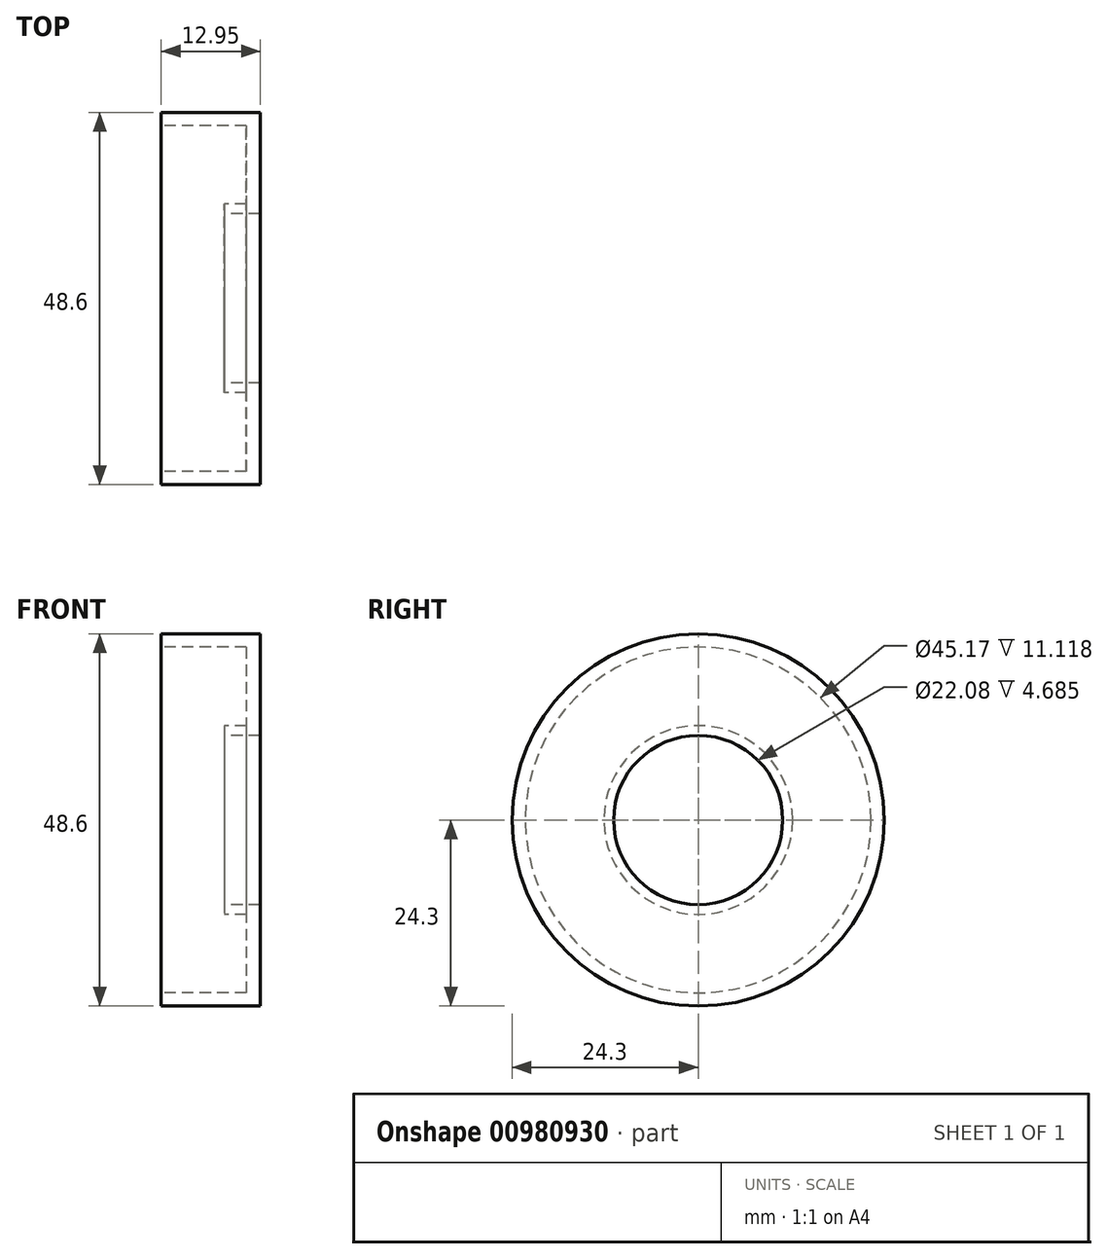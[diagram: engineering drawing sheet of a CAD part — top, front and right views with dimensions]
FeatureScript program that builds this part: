
annotation { "Feature Type Name" : "Feature", "Feature Type Description" : "" }
export const myFeature = defineFeature(function(context is Context, id is Id, definition is map)
    precondition{}
    {
        {
            var Q0;
            Q0=qCreatedBy(makeId("Front.planeOp"),FACE);
            var sketch = newSketch(context, id + "F0", { "sketchPlane" : qUnion([Q0])});
            skLineSegment(sketch, "E0", {"start": v(-81.51, 0) * mm, "end": v(83.97, 0) * mm, "construction": true});
            skLineSegment(sketch, "E1", {"start": v(-12.95, 24.3) * mm, "end": v(0, 24.3) * mm});
            skLineSegment(sketch, "E2", {"start": v(0, 24.3) * mm, "end": v(0, 11.04) * mm});
            skLineSegment(sketch, "E3", {"start": v(0, 11.04) * mm, "end": v(-4.69, 11.04) * mm});
            skLineSegment(sketch, "E4", {"start": v(-4.69, 11.04) * mm, "end": v(-4.69, 12.32) * mm});
            skLineSegment(sketch, "E5", {"start": v(-4.69, 12.32) * mm, "end": v(-1.83, 12.32) * mm});
            skLineSegment(sketch, "E6", {"start": v(-12.95, 24.3) * mm, "end": v(-12.95, 22.59) * mm});
            skLineSegment(sketch, "E7", {"start": v(-12.95, 22.59) * mm, "end": v(-1.83, 22.59) * mm});
            skLineSegment(sketch, "E8", {"start": v(-1.83, 22.59) * mm, "end": v(-1.83, 12.32) * mm});
            skSolve(sketch);
        }
        {
            var Q0;
            Q0 = qSketchRegion(id + "F0", true);
            var Q1;
            Q1=sQuery(id+"F0.wireOp",EDGE,"E0");
            revolve(context, id + "F1", {"surfaceOperationType" : NewSurfaceOperationType.NEW, "entities" : qUnion([Q0]), "axis" : qUnion([Q1]), "revolveType" : RevolveType.FULL});
        }
    });
